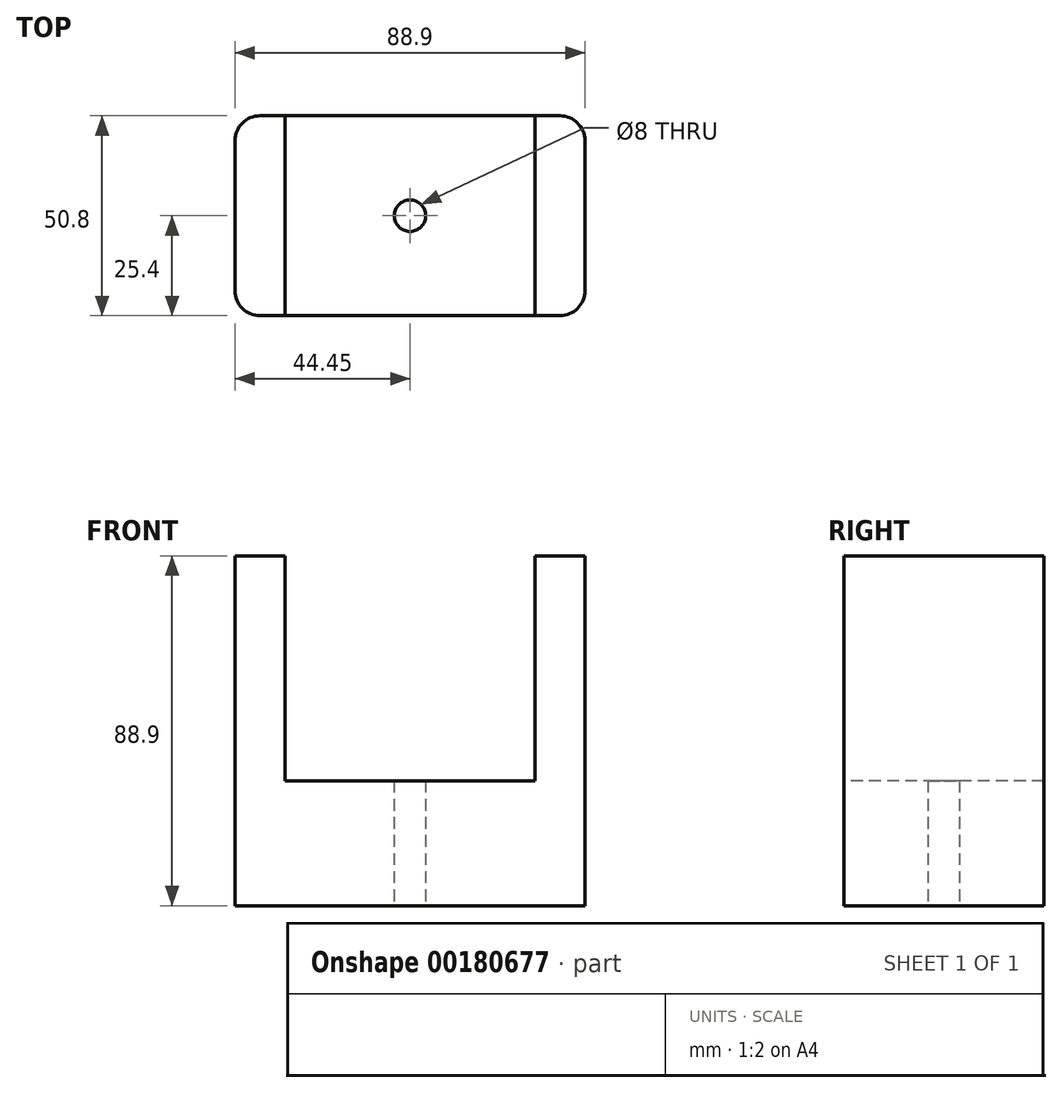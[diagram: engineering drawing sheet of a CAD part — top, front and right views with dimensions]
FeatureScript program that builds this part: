
annotation { "Feature Type Name" : "Feature", "Feature Type Description" : "" }
export const myFeature = defineFeature(function(context is Context, id is Id, definition is map)
    precondition{}
    {
        {
            var Q0;
            Q0=qCreatedBy(makeId("Top.planeOp"),FACE);
            var sketch = newSketch(context, id + "F0", { "sketchPlane" : qUnion([Q0])});
            skLineSegment(sketch, "E0.bottom", {"start": v(38.1, 25.4) * mm, "end": v(-38.1, 25.4) * mm});
            skLineSegment(sketch, "E0.top", {"start": v(38.1, -25.4) * mm, "end": v(-38.1, -25.4) * mm});
            skLineSegment(sketch, "E0.left", {"start": v(44.45, 19.05) * mm, "end": v(44.45, -19.05) * mm});
            skLineSegment(sketch, "E0.right", {"start": v(-44.45, 19.05) * mm, "end": v(-44.45, -19.05) * mm});
            skPoint(sketch, "E0.middle", {"position": v(0, 0) * mm});
            skCircle(sketch, "E1", {"center": v(0, 0) * mm, "radius": 4 * mm});
            skLineSegment(sketch, "E2", {"start": v(-31.75, 25.4) * mm, "end": v(-31.75, -25.4) * mm});
            skLineSegment(sketch, "E3", {"start": v(31.75, -25.4) * mm, "end": v(31.75, 25.4) * mm});
            skPoint(sketch, "E4.visualSharp", {"position": v(-44.45, 25.4) * mm});
            skArc(sketch, "E4.filletArc", {"start": v(-38.1, 25.4) * mm, "mid": v(-42.6, 23.54) * mm, "end": v(-44.45, 19.05) * mm});
            skPoint(sketch, "E5.visualSharp", {"position": v(-44.45, -25.4) * mm});
            skArc(sketch, "E5.filletArc", {"start": v(-44.45, -19.05) * mm, "mid": v(-42.6, -23.54) * mm, "end": v(-38.1, -25.4) * mm});
            skPoint(sketch, "E6.visualSharp", {"position": v(44.45, -25.4) * mm});
            skArc(sketch, "E6.filletArc", {"start": v(38.1, -25.4) * mm, "mid": v(42.6, -23.54) * mm, "end": v(44.45, -19.05) * mm});
            skPoint(sketch, "E7.visualSharp", {"position": v(44.45, 25.4) * mm});
            skArc(sketch, "E7.filletArc", {"start": v(44.45, 19.05) * mm, "mid": v(42.6, 23.54) * mm, "end": v(38.1, 25.4) * mm});
            skSolve(sketch);
        }
        {
            var Q0;
            Q0=makeQuery(id+"F0.imprint","IMPRINT",FACE,{"disambiguationData":[TD([[makeQuery(id+"F0.imprint","IMPRINT",EDGE,{"derivedFrom":sQuery(id+"F0.wireOp",EDGE,"E1")}),-1.0]])]});
            extrude(context, id + "F1", {"entities" : qUnion([Q0]), "depth" : 31.75 * mm});
        }
        {
            var Q0;
            Q0=makeQuery(id+"F0.imprint","IMPRINT",FACE,{"disambiguationData":[TD([[makeQuery(id+"F0.imprint","IMPRINT",EDGE,{"derivedFrom":sQuery(id+"F0.wireOp",EDGE,"E0.right")}),1.0]])]});
            var Q1;
            Q1=makeQuery(id+"F0.imprint","IMPRINT",FACE,{"disambiguationData":[TD([[makeQuery(id+"F0.imprint","IMPRINT",EDGE,{"derivedFrom":sQuery(id+"F0.wireOp",EDGE,"E0.left")}),-1.0]])]});
            extrude(context, id + "F2", {"entities" : qUnion([Q0, Q1]), "operationType" : NewBodyOperationType.ADD, "depth" : 88.9 * mm});
        }
    });
